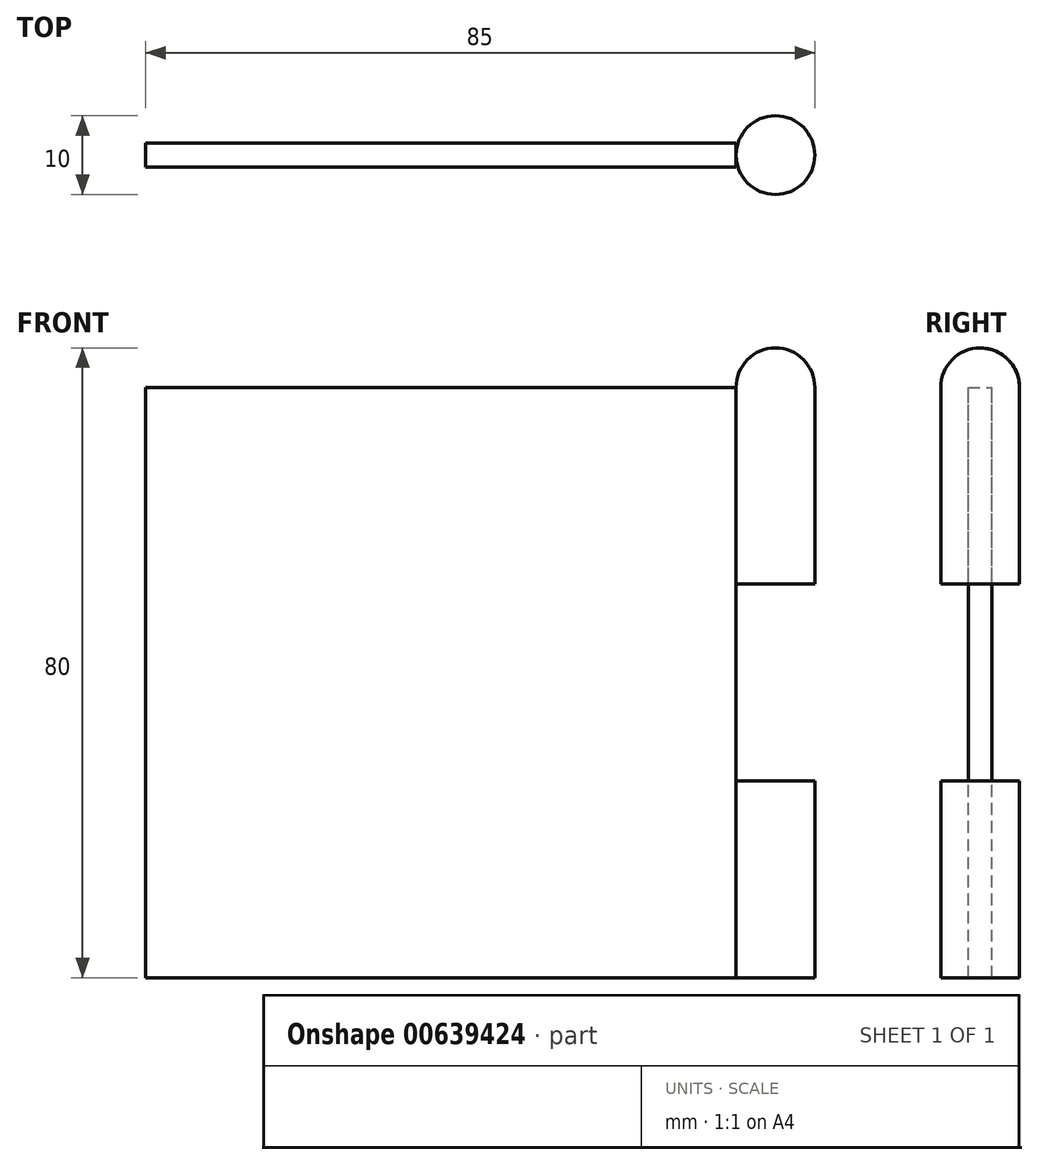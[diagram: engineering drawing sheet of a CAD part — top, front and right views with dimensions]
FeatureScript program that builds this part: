
annotation { "Feature Type Name" : "Feature", "Feature Type Description" : "" }
export const myFeature = defineFeature(function(context is Context, id is Id, definition is map)
    precondition{}
    {
        {
            var Q0;
            Q0=qCreatedBy(makeId("Front.planeOp"),FACE);
            var sketch = newSketch(context, id + "F0", { "sketchPlane" : qUnion([Q0])});
            skLineSegment(sketch, "E0.bottom", {"start": v(0, 0) * mm, "end": v(75, 0) * mm});
            skLineSegment(sketch, "E0.top", {"start": v(0, 75) * mm, "end": v(75, 75) * mm});
            skLineSegment(sketch, "E0.left", {"start": v(0, 0) * mm, "end": v(0, 75) * mm});
            skLineSegment(sketch, "E0.right", {"start": v(75, 0) * mm, "end": v(75, 75) * mm});
            skSolve(sketch);
        }
        {
            var Q0;
            Q0=makeQuery(id+"F0.imprint","IMPRINT",FACE,{"disambiguationData":[TD([[makeQuery(id+"F0.imprint","IMPRINT",EDGE,{"derivedFrom":sQuery(id+"F0.wireOp",EDGE,"E0.bottom")}),1.0]])]});
            extrude(context, id + "F1", {"entities" : qUnion([Q0]), "depth" : 3 * mm, "offsetDistance" : 25 * mm});
        }
        {
            var Q0;
            Q0=qCreatedBy(makeId("Top.planeOp"),FACE);
            var sketch = newSketch(context, id + "F2", { "sketchPlane" : qUnion([Q0])});
            skPoint(sketch, "E1.0", {"position": v(75, -1.5) * mm});
            skLineSegment(sketch, "E2", {"start": v(75, -1.5) * mm, "end": v(80, -1.5) * mm});
            skCircle(sketch, "E3", {"center": v(80, -1.5) * mm, "radius": 5 * mm});
            skSolve(sketch);
        }
        {
            var Q0;
            Q0=makeQuery(id+"F2.imprint","IMPRINT",FACE,{"disambiguationData":[TD([[makeQuery(id+"F2.imprint","IMPRINT",EDGE,{"derivedFrom":sQuery(id+"F2.wireOp",EDGE,"E3")}),1.0]])]});
            extrude(context, id + "F3", {"entities" : qUnion([Q0]), "operationType" : NewBodyOperationType.ADD, "depth" : 25 * mm, "offsetDistance" : 25 * mm});
        }
        {
            var Q0;
            Q0=makeQuery(id+"F1.opExtrude","SWEPT_FACE",FACE,{"disambiguationData":[OSD([sQuery(id+"F0.wireOp",EDGE,"E0.top")])]});
            var sketch = newSketch(context, id + "F4", { "sketchPlane" : qUnion([Q0])});
            skCircle(sketch, "E4.0", {"center": v(80, -1.5) * mm, "radius": 5 * mm});
            skSolve(sketch);
        }
        {
            var Q0;
            Q0=makeQuery(id+"F4.imprint","IMPRINT",FACE,{"disambiguationData":[TD([[makeQuery(id+"F4.imprint","IMPRINT",EDGE,{"derivedFrom":sQuery(id+"F4.wireOp",EDGE,"E4.0")}),1.0]])]});
            extrude(context, id + "F5", {"entities" : qUnion([Q0]), "oppositeDirection" : true, "depth" : 25 * mm, "offsetDistance" : 25 * mm});
        }
        {
            var Q0;
            Q0=qCreatedBy(makeId("Right.planeOp"),FACE);
            cPlane(context, id + "F6", {"entities" : qUnion([Q0]), "cplaneType" : CPlaneType.OFFSET, "offset" : 80 * mm, "width" : 150 * mm, "height" : 150 * mm});
        }
        {
            var Q0;
            Q0=qCreatedBy(id+"F6.planeOp",FACE);
            var sketch = newSketch(context, id + "F7", { "sketchPlane" : qUnion([Q0])});
            skLineSegment(sketch, "E5.0", {"start": v(-6.5, 75) * mm, "end": v(-1.5, 75) * mm});
            skArc(sketch, "E6", {"start": v(-1.5, 80) * mm, "mid": v(-5.04, 78.54) * mm, "end": v(-6.5, 75) * mm});
            skLineSegment(sketch, "E7", {"start": v(-1.5, 80) * mm, "end": v(-1.5, 75) * mm});
            skPoint(sketch, "E8.orphan", {"position": v(3.5, 75) * mm});
            skSolve(sketch);
        }
        {
            var Q0;
            Q0=makeQuery(id+"F7.imprint","IMPRINT",FACE,{"disambiguationData":[TD([[makeQuery(id+"F7.imprint","IMPRINT",EDGE,{"derivedFrom":sQuery(id+"F7.wireOp",EDGE,"E6")}),1.0]])]});
            var Q1;
            Q1=sQuery(id+"F7.wireOp",EDGE,"E7");
            revolve(context, id + "F8", {"operationType" : NewBodyOperationType.ADD, "entities" : qUnion([Q0]), "axis" : qUnion([Q1]), "revolveType" : RevolveType.FULL});
        }
    });
